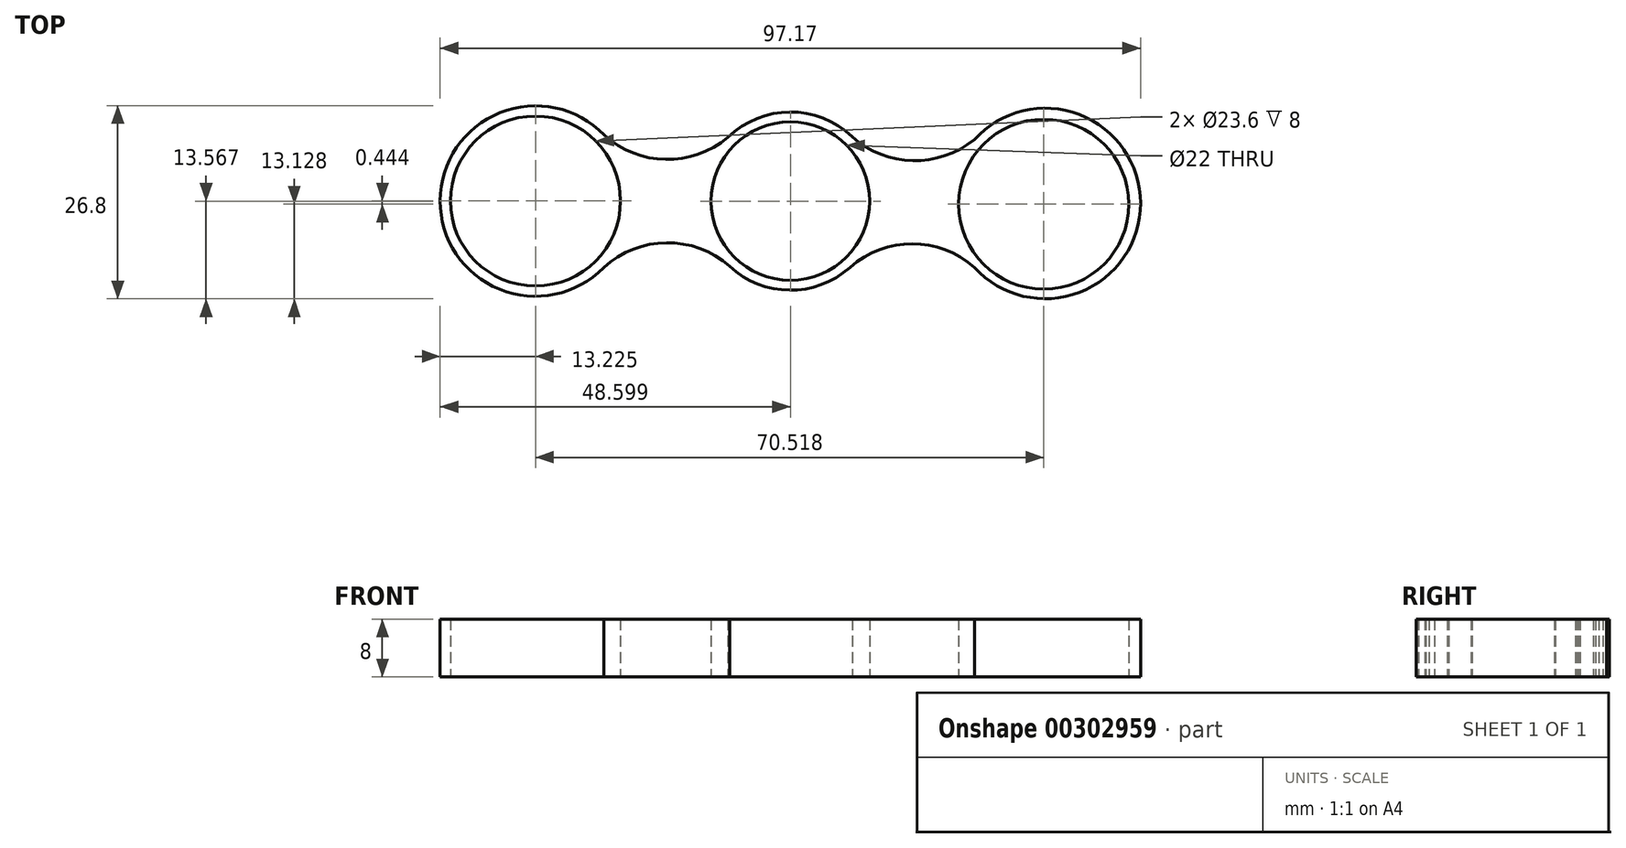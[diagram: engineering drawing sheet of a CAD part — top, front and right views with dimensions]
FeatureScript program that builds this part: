
annotation { "Feature Type Name" : "Feature", "Feature Type Description" : "" }
export const myFeature = defineFeature(function(context is Context, id is Id, definition is map)
    precondition{}
    {
        {
            var Q0;
            Q0=qCreatedBy(makeId("Top.planeOp"),FACE);
            var sketch = newSketch(context, id + "F0", { "sketchPlane" : qUnion([Q0])});
            skCircle(sketch, "E0", {"center": v(-52.03, 26.01) * mm, "radius": 11.38 * mm});
            skCircle(sketch, "E1", {"center": v(18.48, 25.57) * mm, "radius": 11.75 * mm});
            skCircle(sketch, "E2", {"center": v(-16.66, 26) * mm, "radius": 10.81 * mm});
            skLineSegment(sketch, "E3", {"start": v(-52.03, 26.01) * mm, "end": v(-16.66, 26) * mm});
            skLineSegment(sketch, "E4", {"start": v(-16.66, 26) * mm, "end": v(18.48, 25.57) * mm});
            skSolve(sketch);
        }
        {
            var Q0;
            {var subQ0=sQuery(id+"F0.wireOp",EDGE,"eLH46XQA-vSUI-iMd0-sg69-KiP0KIdJpEgJ");var subQ1=sQuery(id+"F0.wireOp",EDGE,"E0");var subQ2=makeQuery(id+"F0.imprint","INTERSECT",VERTEX,{"disambiguationData":[OD(0.0)],"derivedFrom":[subQ1,subQ0]});Q0=makeQuery(id+"F0.imprint","IMPRINT",FACE,{"disambiguationData":[TD([[makeQuery(id+"F0.imprint","IMPRINT",EDGE,{"disambiguationData":[TD([[subQ2,-1.0]])],"derivedFrom":subQ1}),1.0]])]});}
            var Q1;
            {var subQ0=sQuery(id+"F0.wireOp",EDGE,"eLH46XQA-vSUI-iMd0-sg69-KiP0KIdJpEgJ");var subQ1=sQuery(id+"F0.wireOp",EDGE,"E0");var subQ2=makeQuery(id+"F0.imprint","INTERSECT",VERTEX,{"disambiguationData":[OD(1.0)],"derivedFrom":[subQ1,subQ0]});Q1=makeQuery(id+"F0.imprint","IMPRINT",FACE,{"disambiguationData":[TD([[makeQuery(id+"F0.imprint","IMPRINT",EDGE,{"disambiguationData":[TD([[subQ2,1.0]])],"derivedFrom":subQ1}),-1.0]])]});}
            var Q2;
            {var subQ3=sQuery(id+"F0.wireOp",EDGE,"E2");var subQ9=sQuery(id+"F0.wireOp",EDGE,"eLH46XQA-vSUI-iMd0-sg69-KiP0KIdJpEgJ");var subQ11=makeQuery(id+"F0.imprint","INTERSECT",VERTEX,{"disambiguationData":[OD(0.0)],"derivedFrom":[subQ3,subQ9]});Q2=makeQuery(id+"F0.imprint","IMPRINT",FACE,{"disambiguationData":[TD([[makeQuery(id+"F0.imprint","IMPRINT",EDGE,{"disambiguationData":[TD([[subQ11,1.0]])],"derivedFrom":subQ3}),1.0]])]});}
            var Q3;
            {var subQ0=sQuery(id+"F0.wireOp",EDGE,"14d4b4f2-e292-4003-8598-e30e25584506");var subQ1=sQuery(id+"F0.wireOp",EDGE,"E1");var subQ2=makeQuery(id+"F0.imprint","INTERSECT",VERTEX,{"derivedFrom":[subQ1,subQ0]});Q3=makeQuery(id+"F0.imprint","IMPRINT",FACE,{"disambiguationData":[TD([[makeQuery(id+"F0.imprint","IMPRINT",EDGE,{"disambiguationData":[TD([[subQ2,-1.0]])],"derivedFrom":subQ1}),-1.0]])]});}
            var Q4;
            {var subQ0=sQuery(id+"F0.wireOp",EDGE,"787996e5-f360-4557-adc4-2e3b048ffbaa");var subQ1=sQuery(id+"F0.wireOp",EDGE,"E0");var subQ2=makeQuery(id+"F0.imprint","INTERSECT",VERTEX,{"disambiguationData":[OD(1.0)],"derivedFrom":[subQ1,subQ0]});Q4=makeQuery(id+"F0.imprint","IMPRINT",FACE,{"disambiguationData":[TD([[makeQuery(id+"F0.imprint","IMPRINT",EDGE,{"disambiguationData":[TD([[subQ2,-1.0]])],"derivedFrom":subQ1}),-1.0]])]});}
            var Q5;
            {var subQ0=sQuery(id+"F0.wireOp",EDGE,"E4");var subQ1=sQuery(id+"F0.wireOp",EDGE,"E1");var subQ2=makeQuery(id+"F0.imprint","INTERSECT",VERTEX,{"derivedFrom":[subQ1,subQ0]});Q5=makeQuery(id+"F0.imprint","IMPRINT",FACE,{"disambiguationData":[TD([[makeQuery(id+"F0.imprint","IMPRINT",EDGE,{"disambiguationData":[TD([[subQ2,-1.0]])],"derivedFrom":subQ1}),-1.0]])]});}
            var Q6;
            {var subQ1=sQuery(id+"F0.wireOp",EDGE,"E2");var subQ8=makeQuery(id+"F0.imprint","INTERSECT",VERTEX,{"derivedFrom":[subQ1,sQuery(id+"F0.wireOp",EDGE,"787996e5-f360-4557-adc4-2e3b048ffbaa")]});Q6=makeQuery(id+"F0.imprint","IMPRINT",FACE,{"disambiguationData":[TD([[makeQuery(id+"F0.imprint","IMPRINT",EDGE,{"disambiguationData":[TD([[subQ8,1.0]])],"derivedFrom":subQ1}),1.0]])]});}
            var Q7;
            {var subQ0=sQuery(id+"F0.wireOp",EDGE,"eLH46XQA-vSUI-iMd0-sg69-KiP0KIdJpEgJ");var subQ1=sQuery(id+"F0.wireOp",EDGE,"E0");var subQ2=makeQuery(id+"F0.imprint","INTERSECT",VERTEX,{"disambiguationData":[OD(0.0)],"derivedFrom":[subQ1,subQ0]});Q7=makeQuery(id+"F0.imprint","IMPRINT",FACE,{"disambiguationData":[TD([[makeQuery(id+"F0.imprint","IMPRINT",EDGE,{"disambiguationData":[TD([[subQ2,1.0]])],"derivedFrom":subQ1}),1.0]])]});}
            var Q8;
            {var subQ0=sQuery(id+"F0.wireOp",EDGE,"6df8795b-4d59-4b28-b8dd-ebb0e0d917ad");var subQ1=sQuery(id+"F0.wireOp",EDGE,"E2");var subQ2=makeQuery(id+"F0.imprint","INTERSECT",VERTEX,{"disambiguationData":[OD(0.0)],"derivedFrom":[subQ1,subQ0]});Q8=makeQuery(id+"F0.imprint","IMPRINT",FACE,{"disambiguationData":[TD([[makeQuery(id+"F0.imprint","IMPRINT",EDGE,{"disambiguationData":[TD([[subQ2,-1.0]])],"derivedFrom":subQ1}),1.0]])]});}
            var Q9;
            {var subQ0=sQuery(id+"F0.wireOp",EDGE,"6df8795b-4d59-4b28-b8dd-ebb0e0d917ad");var subQ1=sQuery(id+"F0.wireOp",EDGE,"E1");var subQ2=makeQuery(id+"F0.imprint","INTERSECT",VERTEX,{"disambiguationData":[OD(0.0)],"derivedFrom":[subQ1,subQ0]});Q9=makeQuery(id+"F0.imprint","IMPRINT",FACE,{"disambiguationData":[TD([[makeQuery(id+"F0.imprint","IMPRINT",EDGE,{"disambiguationData":[TD([[subQ2,1.0]])],"derivedFrom":subQ1}),1.0]])]});}
            var Q10;
            {var subQ0=sQuery(id+"F0.wireOp",EDGE,"14d4b4f2-e292-4003-8598-e30e25584506");var subQ1=sQuery(id+"F0.wireOp",EDGE,"E2");var subQ2=makeQuery(id+"F0.imprint","INTERSECT",VERTEX,{"disambiguationData":[OD(0.0)],"derivedFrom":[subQ1,subQ0]});Q10=makeQuery(id+"F0.imprint","IMPRINT",FACE,{"disambiguationData":[TD([[makeQuery(id+"F0.imprint","IMPRINT",EDGE,{"disambiguationData":[TD([[subQ2,1.0]])],"derivedFrom":subQ1}),1.0]])]});}
            var Q11;
            {var subQ0=sQuery(id+"F0.wireOp",EDGE,"eLH46XQA-vSUI-iMd0-sg69-KiP0KIdJpEgJ");var subQ1=sQuery(id+"F0.wireOp",EDGE,"E2");var subQ2=makeQuery(id+"F0.imprint","INTERSECT",VERTEX,{"disambiguationData":[OD(0.0)],"derivedFrom":[subQ1,subQ0]});Q11=makeQuery(id+"F0.imprint","IMPRINT",FACE,{"disambiguationData":[TD([[makeQuery(id+"F0.imprint","IMPRINT",EDGE,{"disambiguationData":[TD([[subQ2,-1.0]])],"derivedFrom":subQ1}),1.0]])]});}
            var Q12;
            {var subQ0=sQuery(id+"F0.wireOp",EDGE,"787996e5-f360-4557-adc4-2e3b048ffbaa");var subQ1=sQuery(id+"F0.wireOp",EDGE,"E0");var subQ2=makeQuery(id+"F0.imprint","INTERSECT",VERTEX,{"disambiguationData":[OD(0.0)],"derivedFrom":[subQ1,subQ0]});Q12=makeQuery(id+"F0.imprint","IMPRINT",FACE,{"disambiguationData":[TD([[makeQuery(id+"F0.imprint","IMPRINT",EDGE,{"disambiguationData":[TD([[subQ2,-1.0]])],"derivedFrom":subQ1}),1.0]])]});}
            var Q13;
            {var subQ0=sQuery(id+"F0.wireOp",EDGE,"E1");var subQ1=makeQuery(id+"F0.imprint","INTERSECT",VERTEX,{"derivedFrom":[subQ0,sQuery(id+"F0.wireOp",EDGE,"14d4b4f2-e292-4003-8598-e30e25584506")]});Q13=makeQuery(id+"F0.imprint","IMPRINT",FACE,{"disambiguationData":[TD([[makeQuery(id+"F0.imprint","IMPRINT",EDGE,{"disambiguationData":[TD([[subQ1,-1.0]])],"derivedFrom":subQ0}),1.0]])]});}
            extrude(context, id + "F1", {"entities" : qUnion([Q0, Q1, Q2, Q3, Q4, Q5, Q6, Q7, Q8, Q9, Q10, Q11, Q12, Q13]), "depth" : 8 * mm});
        }
        {
            var Q0;
            Q0=makeQuery(id+"F1.opExtrude","CAP_FACE",FACE,{"disambiguationData":[OSD([sQuery(id+"F0.wireOp",EDGE,"E0"),sQuery(id+"F0.wireOp",EDGE,"E1"),sQuery(id+"F0.wireOp",EDGE,"E2"),sQuery(id+"F0.wireOp",EDGE,"eLH46XQA-vSUI-iMd0-sg69-KiP0KIdJpEgJ"),sQuery(id+"F0.wireOp",EDGE,"787996e5-f360-4557-adc4-2e3b048ffbaa"),sQuery(id+"F0.wireOp",EDGE,"6df8795b-4d59-4b28-b8dd-ebb0e0d917ad"),sQuery(id+"F0.wireOp",EDGE,"14d4b4f2-e292-4003-8598-e30e25584506")])],"isStart":false});
            var sketch = newSketch(context, id + "F2", { "sketchPlane" : qUnion([Q0])});
            skCircle(sketch, "E5", {"center": v(-52.03, 26.01) * mm, "radius": 13.23 * mm});
            skCircle(sketch, "E6", {"center": v(-16.66, 26) * mm, "radius": 12.37 * mm});
            skCircle(sketch, "E7", {"center": v(18.69, 25.67) * mm, "radius": 13.23 * mm});
            skArc(sketch, "E8", {"start": v(-24.84, 16.72) * mm, "mid": v(-33.7, 20.22) * mm, "end": v(-42.57, 16.77) * mm});
            skArc(sketch, "E9", {"start": v(-42.61, 35.29) * mm, "mid": v(-33.76, 31.78) * mm, "end": v(-24.88, 35.24) * mm});
            skArc(sketch, "E10", {"start": v(-8.31, 35.14) * mm, "mid": v(0.56, 31.62) * mm, "end": v(9.46, 35.04) * mm});
            skArc(sketch, "E11", {"start": v(9.15, 16.55) * mm, "mid": v(0.37, 20.06) * mm, "end": v(-8.47, 16.73) * mm});
            skSolve(sketch);
        }
        {
            var Q0;
            {var subQ0=sQuery(id+"F0.wireOp",EDGE,"eLH46XQA-vSUI-iMd0-sg69-KiP0KIdJpEgJ");var subQ1=sQuery(id+"F0.wireOp",EDGE,"E0");var subQ2=makeQuery(id+"F0.imprint","INTERSECT",VERTEX,{"disambiguationData":[OD(0.0)],"derivedFrom":[subQ1,subQ0]});Q0=makeQuery(id+"F0.imprint","IMPRINT",FACE,{"disambiguationData":[TD([[makeQuery(id+"F0.imprint","IMPRINT",EDGE,{"disambiguationData":[TD([[subQ2,-1.0]])],"derivedFrom":subQ1}),1.0]])]});}
            var Q1;
            Q1 = qSketchRegion(id + "F2", true);
            extrude(context, id + "F3", {"entities" : qUnion([Q0, Q1]), "operationType" : NewBodyOperationType.ADD, "depth" : 8 * mm});
        }
        {
            var Q0;
            Q0=sQuery(id+"F0.wireOp",VERTEX,"E3.start");
            var Q1;
            Q1=sQuery(id+"F0.wireOp",VERTEX,"E4.end");
            var Q2;
            Q2=makeQuery(id+"F1.opExtrude","SWEPT_BODY",BODY,{"disambiguationData":[OSD([sQuery(id+"F0.wireOp",EDGE,"E0"),sQuery(id+"F0.wireOp",EDGE,"E1"),sQuery(id+"F0.wireOp",EDGE,"E2"),sQuery(id+"F0.wireOp",EDGE,"eLH46XQA-vSUI-iMd0-sg69-KiP0KIdJpEgJ"),sQuery(id+"F0.wireOp",EDGE,"787996e5-f360-4557-adc4-2e3b048ffbaa"),sQuery(id+"F0.wireOp",EDGE,"6df8795b-4d59-4b28-b8dd-ebb0e0d917ad"),sQuery(id+"F0.wireOp",EDGE,"14d4b4f2-e292-4003-8598-e30e25584506")])]});
            hole(context, id + "F4", {"style" : HoleStyle.SIMPLE, "endStyle" : HoleEndStyle.THROUGH, "oppositeDirection" : true, "holeDiameter" : 23.6 * mm, "tappedDepth" : 12 * mm, "tapClearance" : 3, "locations" : qUnion([Q0, Q1]), "scope" : qUnion([Q2])});
        }
        {
            var Q0;
            Q0=sQuery(id+"F0.wireOp",VERTEX,"E4.start");
            var Q1;
            Q1=makeQuery(id+"F1.opExtrude","SWEPT_BODY",BODY,{"disambiguationData":[OSD([sQuery(id+"F0.wireOp",EDGE,"E0"),sQuery(id+"F0.wireOp",EDGE,"E1"),sQuery(id+"F0.wireOp",EDGE,"E2"),sQuery(id+"F0.wireOp",EDGE,"eLH46XQA-vSUI-iMd0-sg69-KiP0KIdJpEgJ"),sQuery(id+"F0.wireOp",EDGE,"787996e5-f360-4557-adc4-2e3b048ffbaa"),sQuery(id+"F0.wireOp",EDGE,"6df8795b-4d59-4b28-b8dd-ebb0e0d917ad"),sQuery(id+"F0.wireOp",EDGE,"14d4b4f2-e292-4003-8598-e30e25584506")])]});
            hole(context, id + "F5", {"style" : HoleStyle.SIMPLE, "endStyle" : HoleEndStyle.THROUGH, "oppositeDirection" : true, "holeDiameter" : 22 * mm, "tappedDepth" : 12 * mm, "tapClearance" : 3, "locations" : qUnion([Q0]), "scope" : qUnion([Q1])});
        }
    });
